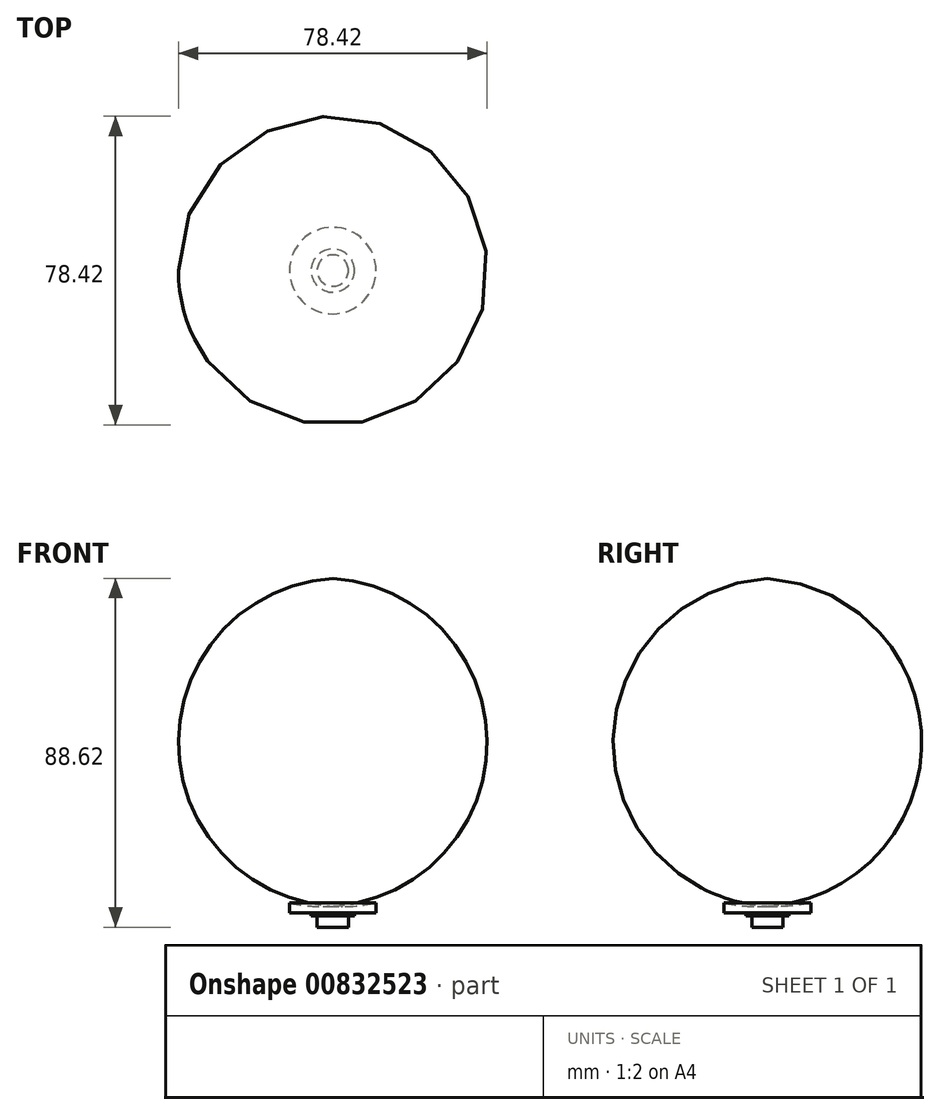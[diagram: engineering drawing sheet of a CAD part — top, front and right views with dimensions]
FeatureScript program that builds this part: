
annotation { "Feature Type Name" : "Feature", "Feature Type Description" : "" }
export const myFeature = defineFeature(function(context is Context, id is Id, definition is map)
    precondition{}
    {
        {
            var Q0;
            Q0=qCreatedBy(makeId("Top.planeOp"),FACE);
            var sketch = newSketch(context, id + "F0", { "sketchPlane" : qUnion([Q0])});
            skCircle(sketch, "E0", {"center": v(0, 0) * mm, "radius": 11 * mm});
            skCircle(sketch, "E1", {"center": v(0, 0) * mm, "radius": 3.98 * mm});
            skCircle(sketch, "E2", {"center": v(0, 0) * mm, "radius": 5.5 * mm});
            skSolve(sketch);
        }
        {
            var Q0;
            Q0=makeQuery(id+"F0.imprint","IMPRINT",FACE,{"disambiguationData":[TD([[makeQuery(id+"F0.imprint","IMPRINT",EDGE,{"derivedFrom":sQuery(id+"F0.wireOp",EDGE,"E1")}),1.0]])]});
            extrude(context, id + "F1", {"entities" : qUnion([Q0]), "oppositeDirection" : true, "depth" : 3.25 * mm, "offsetDistance" : 25 * mm});
        }
        {
            var Q0;
            Q0=makeQuery(id+"F0.imprint","IMPRINT",FACE,{"disambiguationData":[TD([[makeQuery(id+"F0.imprint","IMPRINT",EDGE,{"derivedFrom":sQuery(id+"F0.wireOp",EDGE,"E1")}),-1.0]])]});
            var Q1;
            Q1=makeQuery(id+"F0.imprint","IMPRINT",FACE,{"disambiguationData":[TD([[makeQuery(id+"F0.imprint","IMPRINT",EDGE,{"derivedFrom":sQuery(id+"F0.wireOp",EDGE,"E1")}),1.0]])]});
            extrude(context, id + "F2", {"entities" : qUnion([Q0, Q1]), "operationType" : NewBodyOperationType.ADD, "depth" : 0.4 * mm, "offsetDistance" : 25 * mm, "hasSecondDirection" : true, "secondDirectionOppositeDirection" : true, "secondDirectionDepth" : 0.4 * mm});
        }
        {
            var Q0;
            Q0=qCreatedBy(makeId("Top.planeOp"),FACE);
            cPlane(context, id + "F3", {"entities" : qUnion([Q0]), "cplaneType" : CPlaneType.OFFSET, "offset" : 0.4 * mm, "width" : 150 * mm, "height" : 150 * mm});
        }
        {
            var Q0;
            Q0=qCreatedBy(id+"F3.planeOp",FACE);
            var sketch = newSketch(context, id + "F4", { "sketchPlane" : qUnion([Q0])});
            skCircle(sketch, "E3.0", {"center": v(0, 0) * mm, "radius": 11 * mm});
            skSolve(sketch);
        }
        {
            var Q0;
            Q0 = qSketchRegion(id + "F4", true);
            extrude(context, id + "F5", {"entities" : qUnion([Q0]), "operationType" : NewBodyOperationType.ADD, "depth" : 2.5 * mm, "offsetDistance" : 25 * mm});
        }
        {
            var Q0;
            Q0=qCreatedBy(makeId("Right.planeOp"),FACE);
            var sketch = newSketch(context, id + "F6", { "sketchPlane" : qUnion([Q0])});
            skLineSegment(sketch, "E4", {"start": v(0, 0) * mm, "end": v(0, 2.9) * mm, "construction": true});
            skLineSegment(sketch, "E5.0", {"start": v(-11, 2.9) * mm, "end": v(0, 2.9) * mm});
            skPoint(sketch, "E6.orphan", {"position": v(11, 2.9) * mm});
            skLineSegment(sketch, "E7", {"start": v(0, 2.9) * mm, "end": v(0, 2.1) * mm});
            skArc(sketch, "E8", {"start": v(-11, 2.9) * mm, "mid": v(-5.53, 2.13) * mm, "end": v(0, 2.1) * mm});
            skSolve(sketch);
        }
        {
            var Q0;
            Q0 = qSketchRegion(id + "F6", true);
            var Q1;
            Q1 = qConstructionFilter(qBodyType(qCreatedBy(id + "F6" ,EDGE), BodyType.WIRE), ConstructionObject.NO);
            var Q2;
            Q2=sQuery(id+"F6.wireOp",EDGE,"E4");
            revolve(context, id + "F7", {"operationType" : NewBodyOperationType.REMOVE, "surfaceOperationType" : NewSurfaceOperationType.NEW, "entities" : qUnion([Q0]), "surfaceEntities" : qUnion([Q1]), "axis" : qUnion([Q2]), "revolveType" : RevolveType.FULL, "oppositeDirection" : true});
        }
    });
